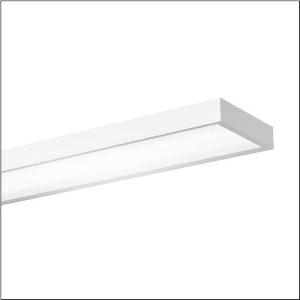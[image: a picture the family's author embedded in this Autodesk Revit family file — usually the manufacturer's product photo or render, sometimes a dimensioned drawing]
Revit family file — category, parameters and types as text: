
# Revit family: sport_31_51hs12dd4jca
name_source: partatom
category: Lighting Fixtures
units: mm (PartAtom-declared; Revit-internal decimal feet)

## family parameters
Cut with Voids When Loaded = No
Host = Face
Light Source = No
Part Type = Normal
Room Calculation Point = No
Round Connector Dimension = Use Diameter
Shared = No

## types (1)
- --- (1 x LED, 19720 lm, 146.2 W, 4000K)
    Apparent Load = 146 VA
    CIE Flux Codes = 65 89 97 100 100
    Color Rendering = 80
    Color Temperature = 4000K
    Default Elevation = 1800 mm
    Description = Sport 31, LED high bay luminaire, primary light control with reflector, of sheet steel, primary anti-glare with prismatic structure, of PC, primary optical cover: cover panel, of PC, light emission: direct distribution, primary light characteristic: symmetric, installation type: suspended mounting, recessed, surface-mounted, LED, rated luminous flux: 20.000lm, luminous efficacy: 137lm/W, light colour: 840, colour temperature: 4000K, control gear: ECG DALI, with terminal, 5-pole, max. 2.5mm², mains connection: 220..240V, AC/DC, 50/60Hz, rated input power: 146W, housing, of sheet steel, traffic white (RAL 9016), length: 1.540mm, width: 415mm, height: 95mm, protection rating (complete): IP20, protection rating (lamp compartment, on room side): IP50, insulation class (complete): insulation class I (protective earthing), certification: CE, ENEC, UKCA, ball protection: ball impact resistant with ceiling mounting or chain suspension, impact resistance: IK08, permissible operating ambient temperature: -20..+35°C, standard: DIN 18032-3, EN 60598-2-22, packaging unit: 1 piece
    Height = 100 mm  [stored 0.328084 ft]
    Lamp = 1 x LED
    Lamp Light Flux = 19720 lm
    Lamp Power = 146.2 W
    Lamp count = 1
    Length = 1500 mm
    Luminous efficacy = 135 lm/W
    Manufacturer = Siteco
    ModVariant = No
    Model = 51HS12DD4JCA
    Mounting Place = Ceiling
    Mounting Type = Pendant
    Number of Poles = 1
    OnlyDefault = Yes
    Power Factor = 1
    Product Name = Sport 31
    Product group = LED high bay luminaire
    ProductGroupID = 903
    Protection Class = Protection class I
    Protection Degree = IP 20
    RLX_Detail_Level = 1
    RLX_Emergency_Light_Flux = 0 lm
    RLX_Emergency_Type = 0
    RLX_Emergency_Type_DB = No
    RlxData = <blob elided: 24153 chars, md5=01a20f75>
    Socket = socket
    Standby Power = 0 W
    System Light Flux = 19719 lm
    System Power = 146 W
    Type Comments = factory setting: luminous flux: 100 % | dim-lin: 254 | 610 mA
    Type Image = l_1006829.jpg
    URL = http://relux.com
    VarID = @adj_150881
    Voltage = 0 V
    Weight = 0.00 kg
    Width = 415 mm

note: [stored X ft] marks values corroborated as IEEE doubles in the binary element streams (Revit-internal decimal feet)

## geometry (parser evidence)
native form markers: Blend x4, Sweep x13
no freeform markers — native parametric forms only
